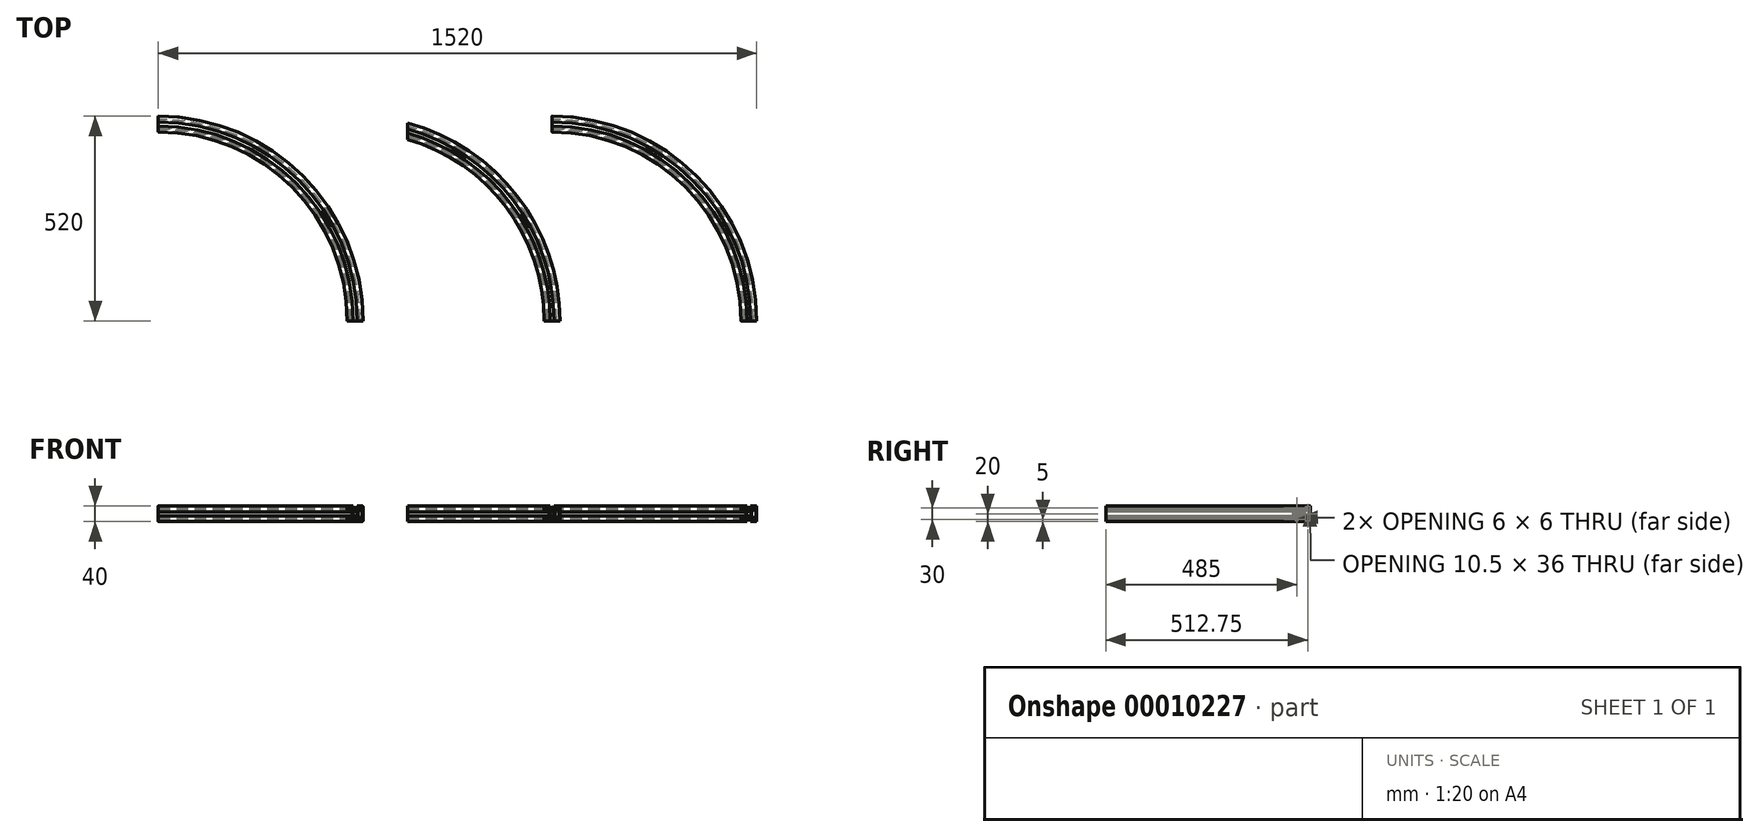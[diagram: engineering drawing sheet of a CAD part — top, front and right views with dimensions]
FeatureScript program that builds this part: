
annotation { "Feature Type Name" : "Feature", "Feature Type Description" : "" }
export const myFeature = defineFeature(function(context is Context, id is Id, definition is map)
    precondition{}
    {
        {
            var Q0;
            Q0=qCreatedBy(makeId("Top.planeOp"),FACE);
            var sketch = newSketch(context, id + "F0", { "sketchPlane" : qUnion([Q0])});
            skLineSegment(sketch, "E0.bottom", {"start": v(0, 0) * mm, "end": v(500, 0) * mm, "construction": true});
            skLineSegment(sketch, "E0.top", {"start": v(0, -500) * mm, "end": v(500, -500) * mm, "construction": true});
            skLineSegment(sketch, "E0.left", {"start": v(0, 0) * mm, "end": v(0, -500) * mm, "construction": true});
            skLineSegment(sketch, "E0.right", {"start": v(500, 0) * mm, "end": v(500, -500) * mm, "construction": true});
            skArc(sketch, "E1", {"start": v(500, -500) * mm, "mid": v(353.55, -146.45) * mm, "end": v(0, 0) * mm});
            skSolve(sketch);
        }
        {
            var Q0;
            Q0=qCreatedBy(makeId("Right.planeOp"),FACE);
            var sketch = newSketch(context, id + "F1", { "sketchPlane" : qUnion([Q0])});
            skLineSegment(sketch, "E2.bottom", {"start": v(17, 40) * mm, "end": v(-17, 40) * mm});
            skLineSegment(sketch, "E2.top", {"start": v(17, 0) * mm, "end": v(-17, 0) * mm});
            skLineSegment(sketch, "E2.left", {"start": v(20, 37) * mm, "end": v(20, 3) * mm});
            skLineSegment(sketch, "E2.right", {"start": v(-20, 37) * mm, "end": v(-20, 3) * mm});
            skPoint(sketch, "E3", {"position": v(0, 0) * mm});
            skPoint(sketch, "E4", {"position": v(20, 20) * mm});
            skCircle(sketch, "E5", {"center": v(0, 20) * mm, "radius": 5.25 * mm});
            skPoint(sketch, "E6.visualSharp", {"position": v(20, 40) * mm});
            skArc(sketch, "E6.filletArc", {"start": v(20, 37) * mm, "mid": v(19.12, 39.12) * mm, "end": v(17, 40) * mm});
            skPoint(sketch, "E7.visualSharp", {"position": v(-20, 40) * mm});
            skArc(sketch, "E7.filletArc", {"start": v(-17, 40) * mm, "mid": v(-19.12, 39.12) * mm, "end": v(-20, 37) * mm});
            skPoint(sketch, "E8.visualSharp", {"position": v(-20, 0) * mm});
            skArc(sketch, "E8.filletArc", {"start": v(-20, 3) * mm, "mid": v(-19.12, 0.88) * mm, "end": v(-17, 0) * mm});
            skPoint(sketch, "E9.visualSharp", {"position": v(20, 0) * mm});
            skArc(sketch, "E9.filletArc", {"start": v(17, 0) * mm, "mid": v(19.12, 0.88) * mm, "end": v(20, 3) * mm});
            skLineSegment(sketch, "E10", {"start": v(5, 40) * mm, "end": v(5, 34.5) * mm});
            skLineSegment(sketch, "E11", {"start": v(5, 34.5) * mm, "end": v(10, 34.5) * mm});
            skLineSegment(sketch, "E12", {"start": v(10, 34.5) * mm, "end": v(10, 32.5) * mm});
            skLineSegment(sketch, "E13", {"start": v(10, 32.5) * mm, "end": v(5, 27.5) * mm});
            skLineSegment(sketch, "E14", {"start": v(5, 27.5) * mm, "end": v(-5, 27.5) * mm});
            skLineSegment(sketch, "E15", {"start": v(-5, 27.5) * mm, "end": v(-10, 32.5) * mm});
            skLineSegment(sketch, "E16", {"start": v(-10, 32.5) * mm, "end": v(-10, 34.5) * mm});
            skLineSegment(sketch, "E17", {"start": v(-10, 34.5) * mm, "end": v(-5, 34.5) * mm});
            skLineSegment(sketch, "E18", {"start": v(-5, 34.5) * mm, "end": v(-5, 40) * mm});
            skPoint(sketch, "E19", {"position": v(0, 27.5) * mm});
            skLineSegment(sketch, "E20.bottom", {"start": v(-13, 32) * mm, "end": v(-17, 32) * mm});
            skLineSegment(sketch, "E20.top", {"start": v(-13, 38) * mm, "end": v(-17, 38) * mm});
            skLineSegment(sketch, "E20.left", {"start": v(-12, 33) * mm, "end": v(-12, 37) * mm});
            skLineSegment(sketch, "E20.right", {"start": v(-18, 33) * mm, "end": v(-18, 37) * mm});
            skPoint(sketch, "E21.visualSharp", {"position": v(-18, 38) * mm});
            skArc(sketch, "E21.filletArc", {"start": v(-17, 38) * mm, "mid": v(-17.7, 37.7) * mm, "end": v(-18, 37) * mm});
            skPoint(sketch, "E22.visualSharp", {"position": v(-18, 32) * mm});
            skArc(sketch, "E22.filletArc", {"start": v(-18, 33) * mm, "mid": v(-17.7, 32.3) * mm, "end": v(-17, 32) * mm});
            skPoint(sketch, "E23.visualSharp", {"position": v(-12, 32) * mm});
            skArc(sketch, "E23.filletArc", {"start": v(-13, 32) * mm, "mid": v(-12.3, 32.3) * mm, "end": v(-12, 33) * mm});
            skPoint(sketch, "E24.visualSharp", {"position": v(-12, 38) * mm});
            skArc(sketch, "E24.filletArc", {"start": v(-12, 37) * mm, "mid": v(-12.3, 37.7) * mm, "end": v(-13, 38) * mm});
            skLineSegment(sketch, "E25.1.0", {"start": v(-20, 25) * mm, "end": v(-14.5, 25) * mm});
            skLineSegment(sketch, "E25.1.1", {"start": v(-14.5, 25) * mm, "end": v(-14.5, 30) * mm});
            skLineSegment(sketch, "E25.1.2", {"start": v(-14.5, 30) * mm, "end": v(-12.5, 30) * mm});
            skLineSegment(sketch, "E25.1.3", {"start": v(-12.5, 30) * mm, "end": v(-7.5, 25) * mm});
            skLineSegment(sketch, "E25.1.4", {"start": v(-7.5, 25) * mm, "end": v(-7.5, 15) * mm});
            skLineSegment(sketch, "E25.1.5", {"start": v(-7.5, 15) * mm, "end": v(-12.5, 10) * mm});
            skLineSegment(sketch, "E25.1.6", {"start": v(-12.5, 10) * mm, "end": v(-14.5, 10) * mm});
            skLineSegment(sketch, "E25.1.7", {"start": v(-14.5, 10) * mm, "end": v(-14.5, 15) * mm});
            skLineSegment(sketch, "E25.1.8", {"start": v(-14.5, 15) * mm, "end": v(-20, 15) * mm});
            skLineSegment(sketch, "E25.1.9", {"start": v(-13, 8) * mm, "end": v(-17, 8) * mm});
            skArc(sketch, "E25.1.10", {"start": v(-17, 8) * mm, "mid": v(-17.7, 7.7) * mm, "end": v(-18, 7) * mm});
            skLineSegment(sketch, "E25.1.11", {"start": v(-18, 7) * mm, "end": v(-18, 3) * mm});
            skArc(sketch, "E25.1.12", {"start": v(-18, 3) * mm, "mid": v(-17.7, 2.3) * mm, "end": v(-17, 2) * mm});
            skLineSegment(sketch, "E25.1.13", {"start": v(-13, 2) * mm, "end": v(-17, 2) * mm});
            skArc(sketch, "E25.1.14", {"start": v(-13, 2) * mm, "mid": v(-12.3, 2.3) * mm, "end": v(-12, 3) * mm});
            skLineSegment(sketch, "E25.1.15", {"start": v(-12, 7) * mm, "end": v(-12, 3) * mm});
            skArc(sketch, "E25.1.16", {"start": v(-12, 7) * mm, "mid": v(-12.3, 7.7) * mm, "end": v(-13, 8) * mm});
            skLineSegment(sketch, "E25.2.0", {"start": v(-5, 0) * mm, "end": v(-5, 5.5) * mm});
            skLineSegment(sketch, "E25.2.1", {"start": v(-5, 5.5) * mm, "end": v(-10, 5.5) * mm});
            skLineSegment(sketch, "E25.2.2", {"start": v(-10, 5.5) * mm, "end": v(-10, 7.5) * mm});
            skLineSegment(sketch, "E25.2.3", {"start": v(-10, 7.5) * mm, "end": v(-5, 12.5) * mm});
            skLineSegment(sketch, "E25.2.4", {"start": v(-5, 12.5) * mm, "end": v(5, 12.5) * mm});
            skLineSegment(sketch, "E25.2.5", {"start": v(5, 12.5) * mm, "end": v(10, 7.5) * mm});
            skLineSegment(sketch, "E25.2.6", {"start": v(10, 7.5) * mm, "end": v(10, 5.5) * mm});
            skLineSegment(sketch, "E25.2.7", {"start": v(10, 5.5) * mm, "end": v(5, 5.5) * mm});
            skLineSegment(sketch, "E25.2.8", {"start": v(5, 5.5) * mm, "end": v(5, 0) * mm});
            skArc(sketch, "E26.1", {"start": v(17, 2) * mm, "mid": v(17.7, 2.3) * mm, "end": v(18, 3) * mm});
            skArc(sketch, "E26.5", {"start": v(18, 37) * mm, "mid": v(17.7, 37.7) * mm, "end": v(17, 38) * mm});
            skLineSegment(sketch, "E27", {"start": v(17, 2) * mm, "end": v(13, 2) * mm});
            skLineSegment(sketch, "E28", {"start": v(12, 3) * mm, "end": v(12, 10.5) * mm});
            skLineSegment(sketch, "E29", {"start": v(12, 10.5) * mm, "end": v(7.5, 15) * mm});
            skLineSegment(sketch, "E30", {"start": v(7.5, 15) * mm, "end": v(7.5, 25) * mm});
            skLineSegment(sketch, "E31", {"start": v(7.5, 25) * mm, "end": v(12, 29.5) * mm});
            skLineSegment(sketch, "E32", {"start": v(12, 29.5) * mm, "end": v(12, 37) * mm});
            skLineSegment(sketch, "E33", {"start": v(13, 38) * mm, "end": v(17, 38) * mm});
            skPoint(sketch, "E34", {"position": v(7.5, 20) * mm});
            skPoint(sketch, "E35.visualSharp", {"position": v(12, 2) * mm});
            skArc(sketch, "E35.filletArc", {"start": v(12, 3) * mm, "mid": v(12.3, 2.3) * mm, "end": v(13, 2) * mm});
            skPoint(sketch, "E36.visualSharp", {"position": v(12, 38) * mm});
            skArc(sketch, "E36.filletArc", {"start": v(13, 38) * mm, "mid": v(12.3, 37.7) * mm, "end": v(12, 37) * mm});
            skLineSegment(sketch, "E37", {"start": v(18, 3) * mm, "end": v(18, 37) * mm});
            skSolve(sketch);
        }
        {
            var Q0;
            Q0=makeQuery(id+"F1.imprint","IMPRINT",FACE,{"disambiguationData":[TD([[makeQuery(id+"F1.imprint","IMPRINT",EDGE,{"derivedFrom":sQuery(id+"F1.wireOp",EDGE,"E2.left")}),-1.0]])]});
            var Q1;
            Q1=sQuery(id+"F0.wireOp",EDGE,"E1");
            sweep(context, id + "F2", {"profiles" : qUnion([Q0]), "path" : qUnion([Q1])});
        }
        {
            var Q0;
            Q0=makeQuery(id+"F2.opSweep","SWEPT_BODY",BODY,{"disambiguationData":[OSD([sQuery(id+"F0.wireOp",EDGE,"E1"),sQuery(id+"F1.wireOp",EDGE,"E2.bottom"),sQuery(id+"F1.wireOp",EDGE,"E2.top"),sQuery(id+"F1.wireOp",EDGE,"E2.left"),sQuery(id+"F1.wireOp",EDGE,"E2.right"),sQuery(id+"F1.wireOp",EDGE,"E5"),sQuery(id+"F1.wireOp",EDGE,"E6.filletArc"),sQuery(id+"F1.wireOp",EDGE,"E7.filletArc"),sQuery(id+"F1.wireOp",EDGE,"E8.filletArc"),sQuery(id+"F1.wireOp",EDGE,"E9.filletArc"),sQuery(id+"F1.wireOp",EDGE,"E10"),sQuery(id+"F1.wireOp",EDGE,"E11"),sQuery(id+"F1.wireOp",EDGE,"E12"),sQuery(id+"F1.wireOp",EDGE,"E13"),sQuery(id+"F1.wireOp",EDGE,"E14"),sQuery(id+"F1.wireOp",EDGE,"E15"),sQuery(id+"F1.wireOp",EDGE,"E16"),sQuery(id+"F1.wireOp",EDGE,"E17"),sQuery(id+"F1.wireOp",EDGE,"E18"),sQuery(id+"F1.wireOp",EDGE,"E20.bottom"),sQuery(id+"F1.wireOp",EDGE,"E20.top"),sQuery(id+"F1.wireOp",EDGE,"E20.left"),sQuery(id+"F1.wireOp",EDGE,"E20.right"),sQuery(id+"F1.wireOp",EDGE,"E21.filletArc"),sQuery(id+"F1.wireOp",EDGE,"E22.filletArc"),sQuery(id+"F1.wireOp",EDGE,"E23.filletArc"),sQuery(id+"F1.wireOp",EDGE,"E24.filletArc"),sQuery(id+"F1.wireOp",EDGE,"E25.1.0"),sQuery(id+"F1.wireOp",EDGE,"E25.1.1"),sQuery(id+"F1.wireOp",EDGE,"E25.1.2"),sQuery(id+"F1.wireOp",EDGE,"E25.1.3"),sQuery(id+"F1.wireOp",EDGE,"E25.1.4"),sQuery(id+"F1.wireOp",EDGE,"E25.1.5"),sQuery(id+"F1.wireOp",EDGE,"E25.1.6"),sQuery(id+"F1.wireOp",EDGE,"E25.1.7"),sQuery(id+"F1.wireOp",EDGE,"E25.1.8"),sQuery(id+"F1.wireOp",EDGE,"E25.1.9"),sQuery(id+"F1.wireOp",EDGE,"E25.1.10"),sQuery(id+"F1.wireOp",EDGE,"E25.1.11"),sQuery(id+"F1.wireOp",EDGE,"E25.1.12"),sQuery(id+"F1.wireOp",EDGE,"E25.1.13"),sQuery(id+"F1.wireOp",EDGE,"E25.1.14"),sQuery(id+"F1.wireOp",EDGE,"E25.1.15"),sQuery(id+"F1.wireOp",EDGE,"E25.1.16"),sQuery(id+"F1.wireOp",EDGE,"E25.2.0"),sQuery(id+"F1.wireOp",EDGE,"E25.2.1"),sQuery(id+"F1.wireOp",EDGE,"E25.2.2"),sQuery(id+"F1.wireOp",EDGE,"E25.2.3"),sQuery(id+"F1.wireOp",EDGE,"E25.2.4"),sQuery(id+"F1.wireOp",EDGE,"E25.2.5"),sQuery(id+"F1.wireOp",EDGE,"E25.2.6"),sQuery(id+"F1.wireOp",EDGE,"E25.2.7"),sQuery(id+"F1.wireOp",EDGE,"E25.2.8"),sQuery(id+"F1.wireOp",EDGE,"E26.1"),sQuery(id+"F1.wireOp",EDGE,"E26.5"),sQuery(id+"F1.wireOp",EDGE,"E27"),sQuery(id+"F1.wireOp",EDGE,"E28"),sQuery(id+"F1.wireOp",EDGE,"E29"),sQuery(id+"F1.wireOp",EDGE,"E30"),sQuery(id+"F1.wireOp",EDGE,"E31"),sQuery(id+"F1.wireOp",EDGE,"E32"),sQuery(id+"F1.wireOp",EDGE,"E33"),sQuery(id+"F1.wireOp",EDGE,"E35.filletArc"),sQuery(id+"F1.wireOp",EDGE,"E36.filletArc"),sQuery(id+"F1.wireOp",EDGE,"E37")])]});
            transform(context, id + "F3", {"entities" : qUnion([Q0]), "transformType" : TransformType.TRANSLATION_3D, "dx" : 500 * mm, "dy" : 0 * mm, "dz" : 0 * mm, "makeCopy" : true});
        }
        {
            var Q0;
            Q0=qCreatedBy(makeId("Top.planeOp"),FACE);
            var sketch = newSketch(context, id + "F4", { "sketchPlane" : qUnion([Q0])});
            skPoint(sketch, "E38.0", {"position": v(500, 20) * mm});
            skLineSegment(sketch, "E39.bottom", {"start": v(500, 20) * mm, "end": v(632.7, 20) * mm});
            skLineSegment(sketch, "E39.top", {"start": v(500, -93.27) * mm, "end": v(632.7, -93.27) * mm});
            skLineSegment(sketch, "E39.left", {"start": v(500, 20) * mm, "end": v(500, -93.27) * mm});
            skLineSegment(sketch, "E39.right", {"start": v(632.7, 20) * mm, "end": v(632.7, -93.27) * mm});
            skSolve(sketch);
        }
        {
            var Q0;
            Q0=makeQuery(id+"F4.imprint","IMPRINT",FACE,{"disambiguationData":[TD([[makeQuery(id+"F4.imprint","IMPRINT",EDGE,{"derivedFrom":sQuery(id+"F4.wireOp",EDGE,"E39.bottom")}),-1.0]])]});
            extrude(context, id + "F5", {"entities" : qUnion([Q0]), "operationType" : NewBodyOperationType.REMOVE, "endBound" : BoundingType.THROUGH_ALL, "depth" : 25 * mm});
        }
        {
            var Q0;
            Q0=makeQuery(id+"F2.opSweep","SWEPT_BODY",BODY,{"disambiguationData":[OSD([sQuery(id+"F0.wireOp",EDGE,"E1"),sQuery(id+"F1.wireOp",EDGE,"E2.bottom"),sQuery(id+"F1.wireOp",EDGE,"E2.top"),sQuery(id+"F1.wireOp",EDGE,"E2.left"),sQuery(id+"F1.wireOp",EDGE,"E2.right"),sQuery(id+"F1.wireOp",EDGE,"E5"),sQuery(id+"F1.wireOp",EDGE,"E6.filletArc"),sQuery(id+"F1.wireOp",EDGE,"E7.filletArc"),sQuery(id+"F1.wireOp",EDGE,"E8.filletArc"),sQuery(id+"F1.wireOp",EDGE,"E9.filletArc"),sQuery(id+"F1.wireOp",EDGE,"E10"),sQuery(id+"F1.wireOp",EDGE,"E11"),sQuery(id+"F1.wireOp",EDGE,"E12"),sQuery(id+"F1.wireOp",EDGE,"E13"),sQuery(id+"F1.wireOp",EDGE,"E14"),sQuery(id+"F1.wireOp",EDGE,"E15"),sQuery(id+"F1.wireOp",EDGE,"E16"),sQuery(id+"F1.wireOp",EDGE,"E17"),sQuery(id+"F1.wireOp",EDGE,"E18"),sQuery(id+"F1.wireOp",EDGE,"E20.bottom"),sQuery(id+"F1.wireOp",EDGE,"E20.top"),sQuery(id+"F1.wireOp",EDGE,"E20.left"),sQuery(id+"F1.wireOp",EDGE,"E20.right"),sQuery(id+"F1.wireOp",EDGE,"E21.filletArc"),sQuery(id+"F1.wireOp",EDGE,"E22.filletArc"),sQuery(id+"F1.wireOp",EDGE,"E23.filletArc"),sQuery(id+"F1.wireOp",EDGE,"E24.filletArc"),sQuery(id+"F1.wireOp",EDGE,"E25.1.0"),sQuery(id+"F1.wireOp",EDGE,"E25.1.1"),sQuery(id+"F1.wireOp",EDGE,"E25.1.2"),sQuery(id+"F1.wireOp",EDGE,"E25.1.3"),sQuery(id+"F1.wireOp",EDGE,"E25.1.4"),sQuery(id+"F1.wireOp",EDGE,"E25.1.5"),sQuery(id+"F1.wireOp",EDGE,"E25.1.6"),sQuery(id+"F1.wireOp",EDGE,"E25.1.7"),sQuery(id+"F1.wireOp",EDGE,"E25.1.8"),sQuery(id+"F1.wireOp",EDGE,"E25.1.9"),sQuery(id+"F1.wireOp",EDGE,"E25.1.10"),sQuery(id+"F1.wireOp",EDGE,"E25.1.11"),sQuery(id+"F1.wireOp",EDGE,"E25.1.12"),sQuery(id+"F1.wireOp",EDGE,"E25.1.13"),sQuery(id+"F1.wireOp",EDGE,"E25.1.14"),sQuery(id+"F1.wireOp",EDGE,"E25.1.15"),sQuery(id+"F1.wireOp",EDGE,"E25.1.16"),sQuery(id+"F1.wireOp",EDGE,"E25.2.0"),sQuery(id+"F1.wireOp",EDGE,"E25.2.1"),sQuery(id+"F1.wireOp",EDGE,"E25.2.2"),sQuery(id+"F1.wireOp",EDGE,"E25.2.3"),sQuery(id+"F1.wireOp",EDGE,"E25.2.4"),sQuery(id+"F1.wireOp",EDGE,"E25.2.5"),sQuery(id+"F1.wireOp",EDGE,"E25.2.6"),sQuery(id+"F1.wireOp",EDGE,"E25.2.7"),sQuery(id+"F1.wireOp",EDGE,"E25.2.8"),sQuery(id+"F1.wireOp",EDGE,"E26.1"),sQuery(id+"F1.wireOp",EDGE,"E26.5"),sQuery(id+"F1.wireOp",EDGE,"E27"),sQuery(id+"F1.wireOp",EDGE,"E28"),sQuery(id+"F1.wireOp",EDGE,"E29"),sQuery(id+"F1.wireOp",EDGE,"E30"),sQuery(id+"F1.wireOp",EDGE,"E31"),sQuery(id+"F1.wireOp",EDGE,"E32"),sQuery(id+"F1.wireOp",EDGE,"E33"),sQuery(id+"F1.wireOp",EDGE,"E35.filletArc"),sQuery(id+"F1.wireOp",EDGE,"E36.filletArc"),sQuery(id+"F1.wireOp",EDGE,"E37")])]});
            transform(context, id + "F6", {"entities" : qUnion([Q0]), "transformType" : TransformType.TRANSLATION_3D, "dx" : 1000 * mm, "dy" : 0 * mm, "dz" : 0 * mm, "makeCopy" : true});
        }
    });
